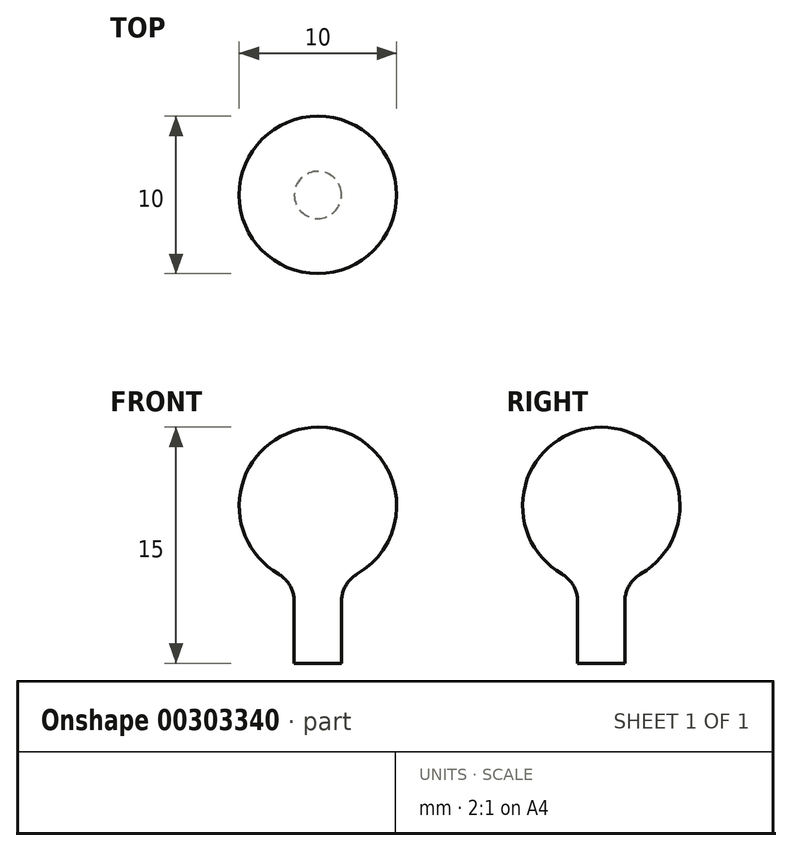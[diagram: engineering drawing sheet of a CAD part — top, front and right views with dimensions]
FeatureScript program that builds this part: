
annotation { "Feature Type Name" : "Feature", "Feature Type Description" : "" }
export const myFeature = defineFeature(function(context is Context, id is Id, definition is map)
    precondition{}
    {
        {
            var Q0;
            Q0=qCreatedBy(makeId("Front.planeOp"),FACE);
            var sketch = newSketch(context, id + "F0", { "sketchPlane" : qUnion([Q0])});
            skArc(sketch, "E0", {"start": v(1.5, -4.77) * mm, "mid": v(4.94, 0.76) * mm, "end": v(0, 5) * mm});
            skLineSegment(sketch, "E1.top", {"start": v(0, -10) * mm, "end": v(1.5, -10) * mm});
            skLineSegment(sketch, "E1.right", {"start": v(1.5, -4.77) * mm, "end": v(1.5, -10) * mm});
            skLineSegment(sketch, "E2", {"start": v(0, 5) * mm, "end": v(0, -10) * mm});
            skSolve(sketch);
        }
        {
            var Q0;
            Q0 = qSketchRegion(id + "F0", true);
            var Q1;
            Q1=sQuery(id+"F0.wireOp",EDGE,"E2");
            revolve(context, id + "F1", {"entities" : qUnion([Q0]), "axis" : qUnion([Q1]), "revolveType" : RevolveType.FULL});
        }
        {
            var Q0;
            Q0=makeQuery(id+"F1.opRevolve","SWEPT_EDGE",EDGE,{"disambiguationData":[OSD([sQuery(id+"F0.wireOp",EDGE,"E0"),sQuery(id+"F0.wireOp",EDGE,"E1.right")])]});
            fillet(context, id + "F2", {"entities" : qUnion([Q0]), "radius" : 2 * mm, "tangentPropagation" : true, "allowEdgeOverflow" : false});
        }
    });
